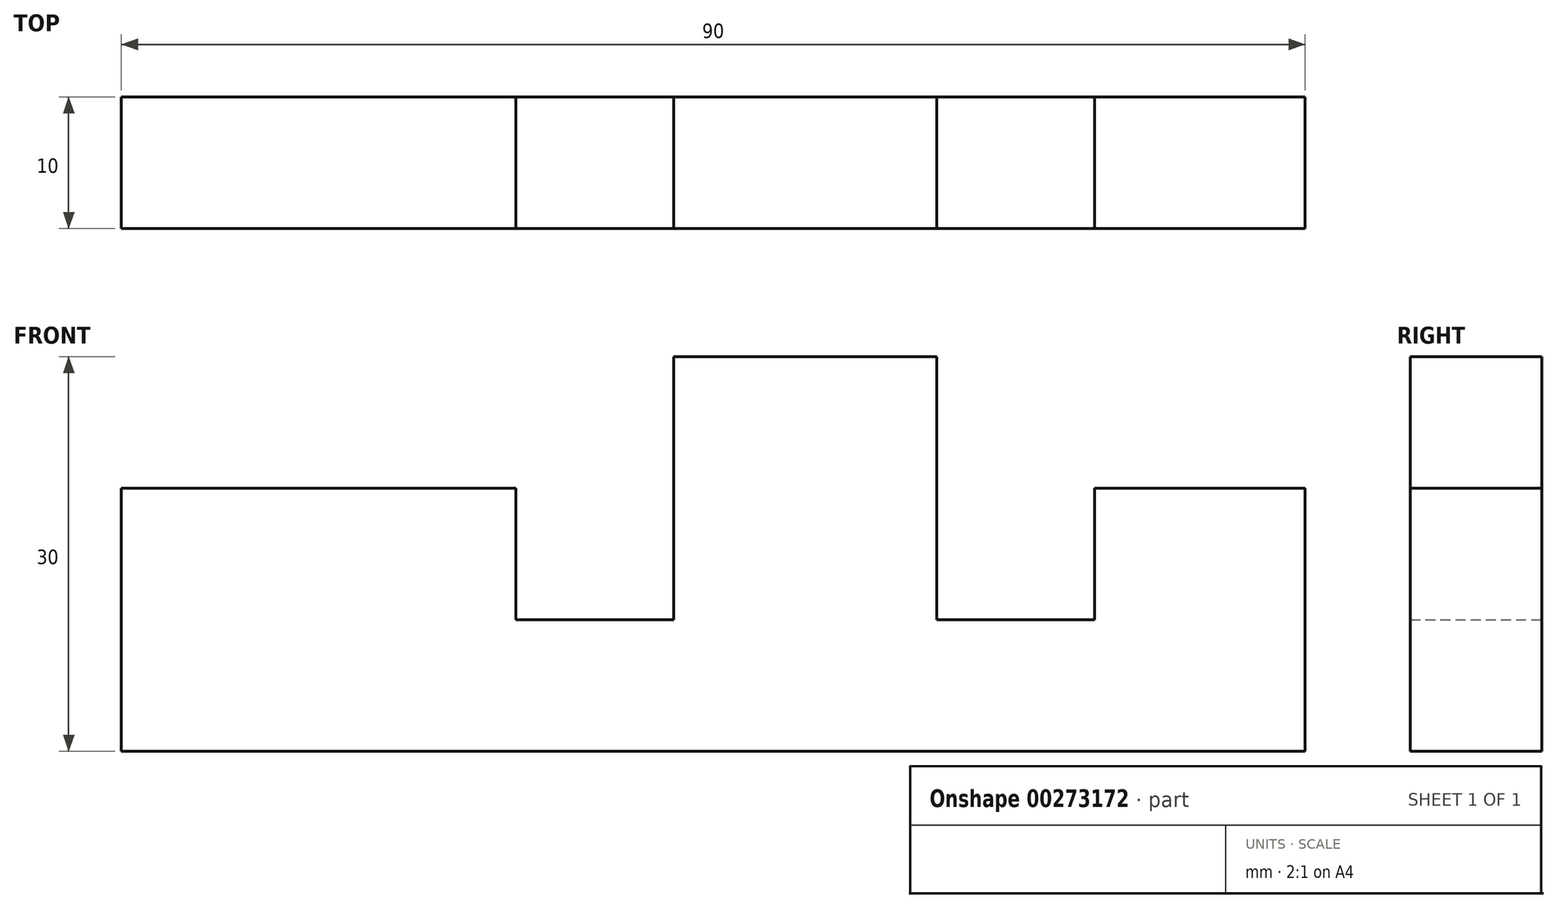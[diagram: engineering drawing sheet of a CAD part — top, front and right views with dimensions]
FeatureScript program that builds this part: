
annotation { "Feature Type Name" : "Feature", "Feature Type Description" : "" }
export const myFeature = defineFeature(function(context is Context, id is Id, definition is map)
    precondition{}
    {
        {
            var Q0;
            Q0=qCreatedBy(makeId("Front.planeOp"),FACE);
            var sketch = newSketch(context, id + "F0", { "sketchPlane" : qUnion([Q0])});
            skLineSegment(sketch, "E0", {"start": v(0, 0) * mm, "end": v(90, 0) * mm});
            skLineSegment(sketch, "E1", {"start": v(0, 0) * mm, "end": v(0, 20) * mm});
            skLineSegment(sketch, "E2", {"start": v(0, 20) * mm, "end": v(30, 20) * mm});
            skLineSegment(sketch, "E3", {"start": v(30, 20) * mm, "end": v(30, 10) * mm});
            skLineSegment(sketch, "E4", {"start": v(30, 10) * mm, "end": v(42, 10) * mm});
            skLineSegment(sketch, "E5", {"start": v(42, 10) * mm, "end": v(42, 30) * mm});
            skLineSegment(sketch, "E6", {"start": v(42, 30) * mm, "end": v(62, 30) * mm});
            skLineSegment(sketch, "E7", {"start": v(62, 30) * mm, "end": v(62, 10) * mm});
            skLineSegment(sketch, "E8", {"start": v(62, 10) * mm, "end": v(74, 10) * mm});
            skLineSegment(sketch, "E9", {"start": v(74, 10) * mm, "end": v(74, 20) * mm});
            skLineSegment(sketch, "E10", {"start": v(74, 20) * mm, "end": v(90, 20) * mm});
            skLineSegment(sketch, "E11", {"start": v(90, 20) * mm, "end": v(90, 0) * mm});
            skLineSegment(sketch, "E12", {"start": v(30, 20) * mm, "end": v(74, 20) * mm, "construction": true});
            skSolve(sketch);
        }
        {
            var Q0;
            Q0 = qSketchRegion(id + "F0", true);
            extrude(context, id + "F1", {"entities" : qUnion([Q0]), "depth" : 10 * mm});
        }
    });
